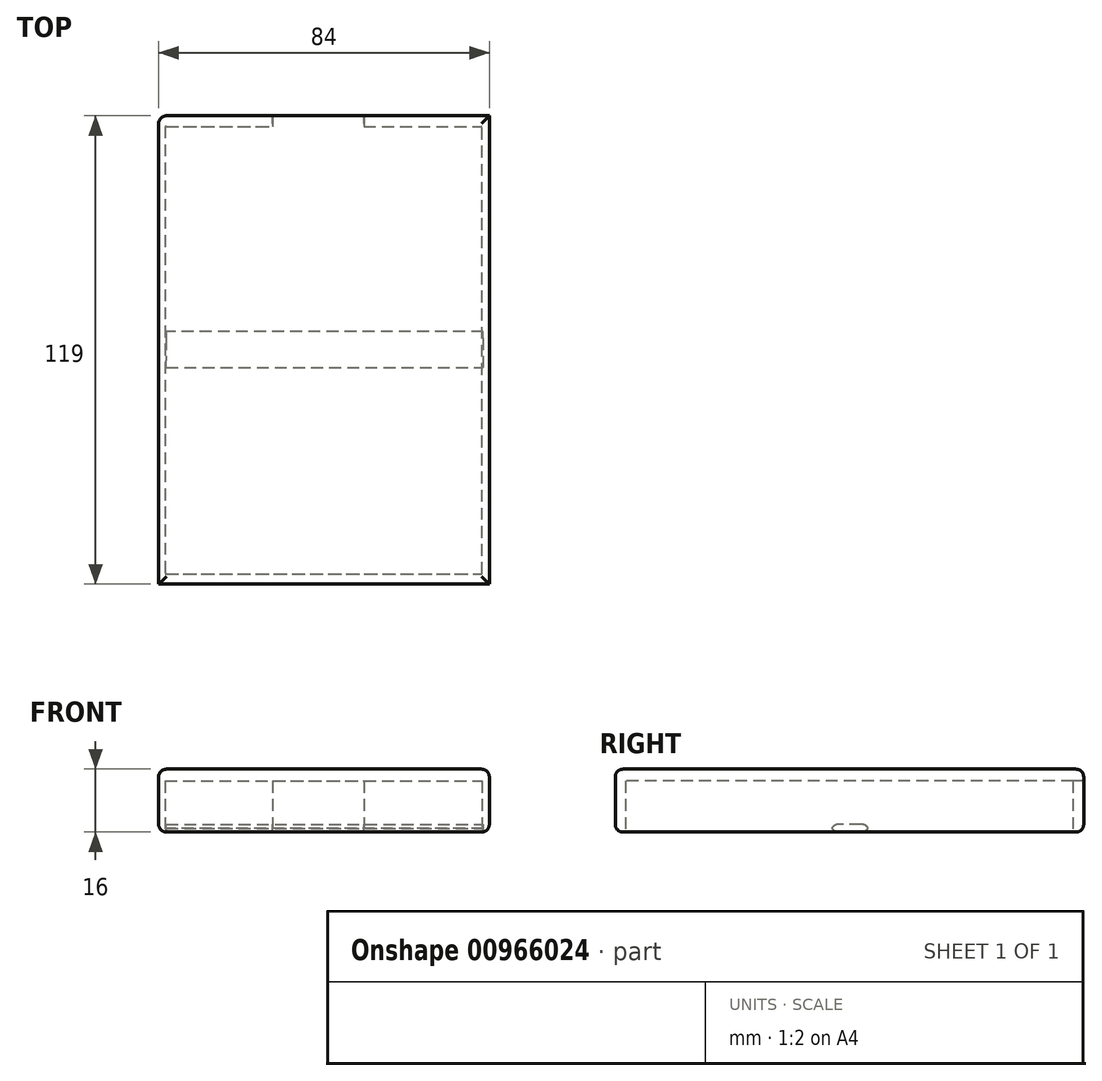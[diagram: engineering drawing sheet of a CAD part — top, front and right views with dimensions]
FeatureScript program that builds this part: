
annotation { "Feature Type Name" : "Feature", "Feature Type Description" : "" }
export const myFeature = defineFeature(function(context is Context, id is Id, definition is map)
    precondition{}
    {
        {
            var Q0;
            Q0=qCreatedBy(makeId("Top.planeOp"),FACE);
            var sketch = newSketch(context, id + "F0", { "sketchPlane" : qUnion([Q0])});
            skLineSegment(sketch, "E0.bottom", {"start": v(-22.84, 46.7) * mm, "end": v(61.16, 46.7) * mm});
            skLineSegment(sketch, "E0.top", {"start": v(-22.84, -72.3) * mm, "end": v(61.16, -72.3) * mm});
            skLineSegment(sketch, "E0.left", {"start": v(-22.84, 46.7) * mm, "end": v(-22.84, -72.3) * mm});
            skLineSegment(sketch, "E0.right", {"start": v(61.16, 46.7) * mm, "end": v(61.16, -72.3) * mm});
            skSolve(sketch);
        }
        {
            var Q0;
            Q0 = qSketchRegion(id + "F0", true);
            extrude(context, id + "F1", {"entities" : qUnion([Q0]), "depth" : 16 * mm, "offsetDistance" : 25 * mm});
        }
        {
            var Q0;
            Q0=qCreatedBy(makeId("Top.planeOp"),FACE);
            var sketch = newSketch(context, id + "F2", { "sketchPlane" : qUnion([Q0])});
            skLineSegment(sketch, "E1.bottom", {"start": v(-21.22, 44) * mm, "end": v(59.28, 44) * mm});
            skLineSegment(sketch, "E1.top", {"start": v(-21.22, -69.71) * mm, "end": v(59.28, -69.71) * mm});
            skLineSegment(sketch, "E1.left", {"start": v(-21.22, 44) * mm, "end": v(-21.22, -69.71) * mm});
            skLineSegment(sketch, "E1.right", {"start": v(59.28, 44) * mm, "end": v(59.28, -69.71) * mm});
            skLineSegment(sketch, "E2.bottom", {"start": v(6.06, 49.33) * mm, "end": v(29.31, 49.33) * mm});
            skLineSegment(sketch, "E2.top", {"start": v(6.06, 44) * mm, "end": v(29.31, 44) * mm});
            skLineSegment(sketch, "E2.left", {"start": v(6.06, 49.33) * mm, "end": v(6.06, 44) * mm});
            skLineSegment(sketch, "E2.right", {"start": v(29.31, 49.33) * mm, "end": v(29.31, 44) * mm});
            skSolve(sketch);
        }
        {
            var Q0;
            Q0 = qSketchRegion(id + "F2", true);
            extrude(context, id + "F3", {"entities" : qUnion([Q0]), "operationType" : NewBodyOperationType.REMOVE, "depth" : 13 * mm, "offsetDistance" : 25 * mm});
        }
        {
            var Q0;
            Q0=makeQuery(id+"F1.opExtrude","CAP_EDGE",EDGE,{"disambiguationData":[OSD([sQuery(id+"F0.wireOp",EDGE,"E0.right")])],"isStart":false});
            var Q1;
            Q1=makeQuery(id+"F1.opExtrude","CAP_EDGE",EDGE,{"disambiguationData":[OSD([sQuery(id+"F0.wireOp",EDGE,"E0.top")])],"isStart":false});
            var Q2;
            Q2=makeQuery(id+"F1.opExtrude","CAP_EDGE",EDGE,{"disambiguationData":[OSD([sQuery(id+"F0.wireOp",EDGE,"E0.left")])],"isStart":false});
            var Q3;
            {var subQ0=sQuery(id+"F0.wireOp",EDGE,"E0.bottom");var subQ1=sQuery(id+"F0.wireOp",EDGE,"E0.right");Q3=makeQuery(id+"F3.boolean.opBoolean","SPLIT",EDGE,{"disambiguationData":[TD([makeQuery(id+"F1.opExtrude","SWEPT_FACE",FACE,{"disambiguationData":[OSD([subQ1])]})])],"derivedFrom":makeQuery(id+"F1.opExtrude","CAP_EDGE",EDGE,{"disambiguationData":[OSD([subQ0])],"isStart":false})});}
            var Q4;
            {var subQ0=sQuery(id+"F0.wireOp",EDGE,"E0.bottom");var subQ1=sQuery(id+"F0.wireOp",EDGE,"E0.left");Q4=makeQuery(id+"F3.boolean.opBoolean","SPLIT",EDGE,{"disambiguationData":[TD([makeQuery(id+"F1.opExtrude","SWEPT_FACE",FACE,{"disambiguationData":[OSD([subQ1])]})])],"derivedFrom":makeQuery(id+"F1.opExtrude","CAP_EDGE",EDGE,{"disambiguationData":[OSD([subQ0])],"isStart":false})});}
            var Q5;
            {var subQ0=sQuery(id+"F0.wireOp",EDGE,"E0.bottom");var subQ1=sQuery(id+"F0.wireOp",EDGE,"E0.left");Q5=makeQuery(id+"F3.boolean.opBoolean","SPLIT",EDGE,{"disambiguationData":[TD([makeQuery(id+"F1.opExtrude","SWEPT_FACE",FACE,{"disambiguationData":[OSD([subQ1])]})])],"derivedFrom":makeQuery(id+"F1.opExtrude","CAP_EDGE",EDGE,{"disambiguationData":[OSD([subQ0])],"isStart":true})});}
            fillet(context, id + "F4", {"entities" : qUnion([Q0, Q1, Q2, Q3, Q4, Q5]), "radius" : 2 * mm, "tangentPropagation" : true, "allowEdgeOverflow" : false});
        }
        {
            var Q0;
            Q0=makeQuery(id+"F1.opExtrude","CAP_EDGE",EDGE,{"disambiguationData":[OSD([sQuery(id+"F0.wireOp",EDGE,"E0.left")])],"isStart":true});
            var Q1;
            Q1=makeQuery(id+"F1.opExtrude","CAP_EDGE",EDGE,{"disambiguationData":[OSD([sQuery(id+"F0.wireOp",EDGE,"E0.top")])],"isStart":true});
            var Q2;
            Q2=makeQuery(id+"F1.opExtrude","CAP_EDGE",EDGE,{"disambiguationData":[OSD([sQuery(id+"F0.wireOp",EDGE,"E0.right")])],"isStart":true});
            var Q3;
            {var subQ0=sQuery(id+"F0.wireOp",EDGE,"E0.bottom");var subQ1=sQuery(id+"F0.wireOp",EDGE,"E0.right");Q3=makeQuery(id+"F3.boolean.opBoolean","SPLIT",EDGE,{"disambiguationData":[TD([makeQuery(id+"F1.opExtrude","SWEPT_FACE",FACE,{"disambiguationData":[OSD([subQ1])]})])],"derivedFrom":makeQuery(id+"F1.opExtrude","CAP_EDGE",EDGE,{"disambiguationData":[OSD([subQ0])],"isStart":true})});}
            fillet(context, id + "F5", {"entities" : qUnion([Q0, Q1, Q2, Q3]), "radius" : 2 * mm, "tangentPropagation" : true, "allowEdgeOverflow" : false});
        }
        {
            var Q0;
            Q0=qCreatedBy(makeId("Top.planeOp"),FACE);
            var sketch = newSketch(context, id + "F6", { "sketchPlane" : qUnion([Q0])});
            skLineSegment(sketch, "E3", {"start": v(-20.9, -7.79) * mm, "end": v(59.6, -7.79) * mm});
            skLineSegment(sketch, "E4", {"start": v(-20.9, -17.53) * mm, "end": v(59.57, -17.53) * mm});
            skLineSegment(sketch, "E5", {"start": v(-20.9, -7.79) * mm, "end": v(-20.9, -17.53) * mm});
            skLineSegment(sketch, "E6", {"start": v(59.6, -7.79) * mm, "end": v(59.57, -17.53) * mm});
            skSolve(sketch);
        }
        {
            var Q0;
            Q0 = qSketchRegion(id + "F6", true);
            extrude(context, id + "F7", {"entities" : qUnion([Q0]), "depth" : 2 * mm, "offsetDistance" : 25 * mm});
        }
        {
            var Q0;
            Q0=makeQuery(id+"F7.opExtrude","CAP_EDGE",EDGE,{"disambiguationData":[OSD([sQuery(id+"F6.wireOp",EDGE,"E4")])],"isStart":true});
            var Q1;
            Q1=makeQuery(id+"F7.opExtrude","CAP_EDGE",EDGE,{"disambiguationData":[OSD([sQuery(id+"F6.wireOp",EDGE,"E3")])],"isStart":true});
            var Q2;
            Q2=makeQuery(id+"F7.opExtrude","CAP_EDGE",EDGE,{"disambiguationData":[OSD([sQuery(id+"F6.wireOp",EDGE,"E3")])],"isStart":false});
            var Q3;
            Q3=makeQuery(id+"F7.opExtrude","CAP_EDGE",EDGE,{"disambiguationData":[OSD([sQuery(id+"F6.wireOp",EDGE,"E4")])],"isStart":false});
            fillet(context, id + "F8", {"entities" : qUnion([Q0, Q1, Q2, Q3]), "radius" : 2 * mm, "tangentPropagation" : true, "allowEdgeOverflow" : false});
        }
    });
